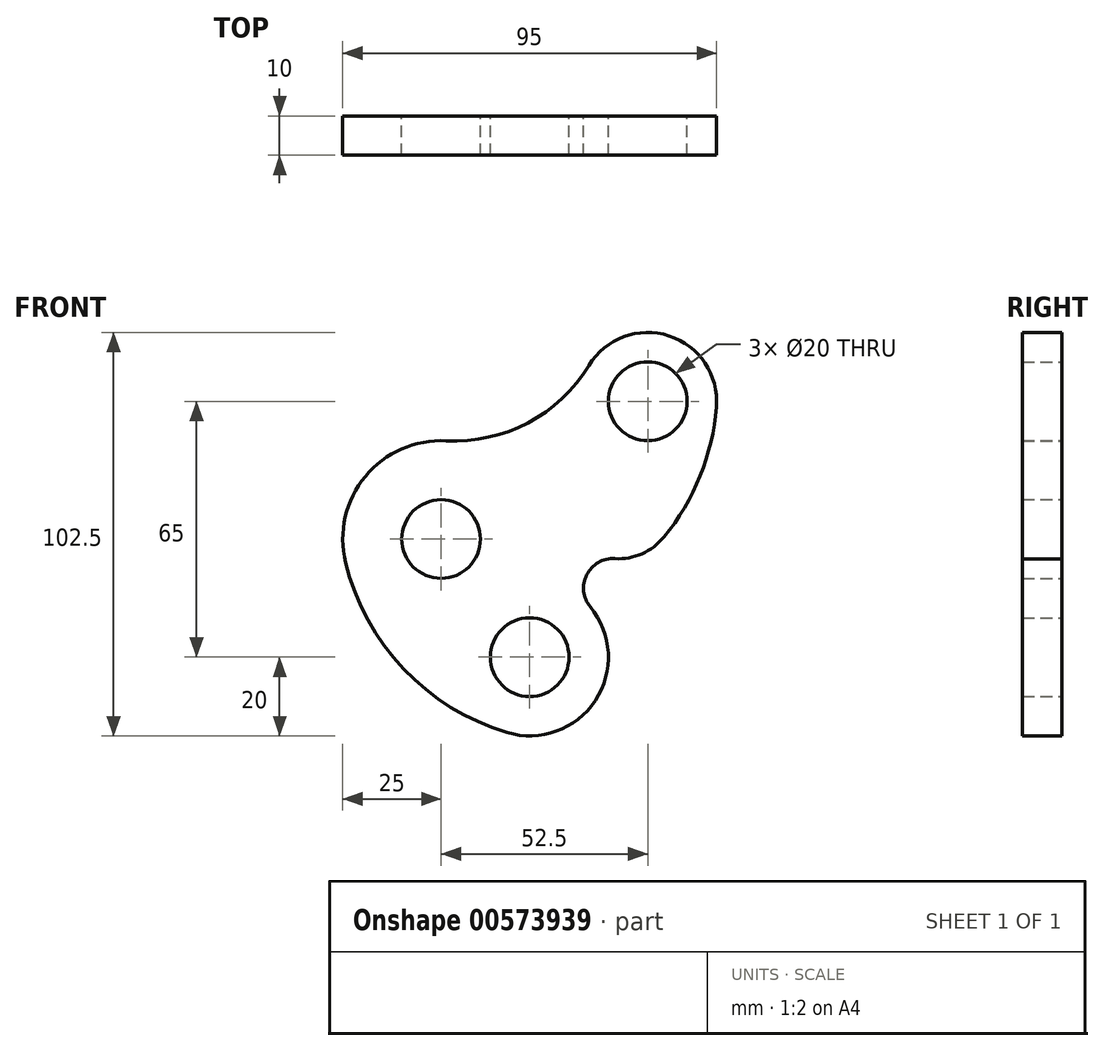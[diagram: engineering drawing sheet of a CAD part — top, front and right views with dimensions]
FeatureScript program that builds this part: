
annotation { "Feature Type Name" : "Feature", "Feature Type Description" : "" }
export const myFeature = defineFeature(function(context is Context, id is Id, definition is map)
    precondition{}
    {
        {
            var Q0;
            Q0=qCreatedBy(makeId("Front.planeOp"),FACE);
            var sketch = newSketch(context, id + "F0", { "sketchPlane" : qUnion([Q0])});
            skCircle(sketch, "E0", {"center": v(0, 0) * mm, "radius": 10 * mm});
            skCircle(sketch, "E1", {"center": v(-22.5, 30) * mm, "radius": 10 * mm});
            skCircle(sketch, "E2", {"center": v(30, 65) * mm, "radius": 10 * mm});
            skArc(sketch, "E3", {"start": v(-21.2, 54.97) * mm, "mid": v(-41.76, 45.94) * mm, "end": v(-46.78, 24.06) * mm});
            skArc(sketch, "E4", {"start": v(-5.75, -19.16) * mm, "mid": v(16.67, -11.05) * mm, "end": v(15.4, 12.76) * mm});
            skArc(sketch, "E5", {"start": v(47.44, 63.58) * mm, "mid": v(35.4, 81.64) * mm, "end": v(15.05, 74.1) * mm});
            skArc(sketch, "E6", {"start": v(-46.78, 24.06) * mm, "mid": v(-32.01, -3) * mm, "end": v(-5.75, -19.16) * mm});
            skArc(sketch, "E7", {"start": v(-21.2, 54.97) * mm, "mid": v(-0.43, 59.54) * mm, "end": v(15.05, 74.1) * mm});
            skArc(sketch, "E8", {"start": v(21.62, 25.03) * mm, "mid": v(14.5, 20.93) * mm, "end": v(15.4, 12.76) * mm});
            skArc(sketch, "E9", {"start": v(21.62, 25.03) * mm, "mid": v(28.53, 26.27) * mm, "end": v(34.12, 30.51) * mm});
            skArc(sketch, "E10", {"start": v(34.12, 30.51) * mm, "mid": v(43.3, 46.03) * mm, "end": v(47.44, 63.58) * mm});
            skSolve(sketch);
        }
        {
            var Q0;
            Q0 = qSketchRegion(id + "F0", true);
            extrude(context, id + "F1", {"entities" : qUnion([Q0]), "depth" : 10 * mm, "offsetDistance" : 25 * mm});
        }
    });
